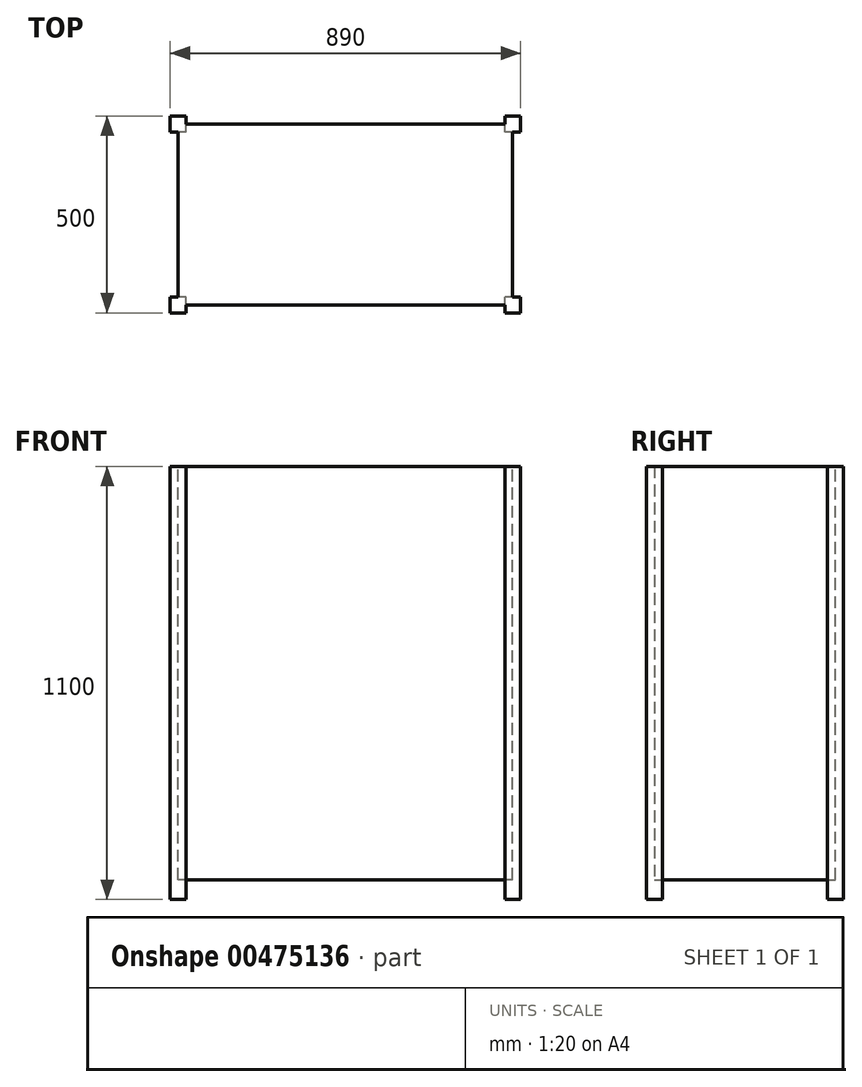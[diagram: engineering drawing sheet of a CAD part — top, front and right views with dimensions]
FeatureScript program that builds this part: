
annotation { "Feature Type Name" : "Feature", "Feature Type Description" : "" }
export const myFeature = defineFeature(function(context is Context, id is Id, definition is map)
    precondition{}
    {
        {
            var Q0;
            Q0=qCreatedBy(makeId("Top.planeOp"),FACE);
            var sketch = newSketch(context, id + "F0", { "sketchPlane" : qUnion([Q0])});
            skLineSegment(sketch, "E0.bottom", {"start": v(425, -230) * mm, "end": v(-425, -230) * mm, "construction": true});
            skLineSegment(sketch, "E0.top", {"start": v(425, 230) * mm, "end": v(-425, 230) * mm, "construction": true});
            skLineSegment(sketch, "E0.left", {"start": v(425, -230) * mm, "end": v(425, 230) * mm, "construction": true});
            skLineSegment(sketch, "E0.right", {"start": v(-425, -230) * mm, "end": v(-425, 230) * mm, "construction": true});
            skPoint(sketch, "E0.middle", {"position": v(0, 0) * mm});
            skLineSegment(sketch, "E1.bottom", {"start": v(-405, 210) * mm, "end": v(-445, 210) * mm});
            skLineSegment(sketch, "E1.top", {"start": v(-405, 250) * mm, "end": v(-445, 250) * mm});
            skLineSegment(sketch, "E1.left", {"start": v(-405, 210) * mm, "end": v(-405, 250) * mm});
            skLineSegment(sketch, "E1.right", {"start": v(-445, 210) * mm, "end": v(-445, 250) * mm});
            skPoint(sketch, "E1.middle", {"position": v(-425, 230) * mm});
            skLineSegment(sketch, "E2.bottom", {"start": v(-405, -250) * mm, "end": v(-445, -250) * mm});
            skLineSegment(sketch, "E2.top", {"start": v(-405, -210) * mm, "end": v(-445, -210) * mm});
            skLineSegment(sketch, "E2.left", {"start": v(-405, -250) * mm, "end": v(-405, -210) * mm});
            skLineSegment(sketch, "E2.right", {"start": v(-445, -250) * mm, "end": v(-445, -210) * mm});
            skPoint(sketch, "E2.middle", {"position": v(-425, -230) * mm});
            skLineSegment(sketch, "E3.bottom", {"start": v(445, 210) * mm, "end": v(405, 210) * mm});
            skLineSegment(sketch, "E3.top", {"start": v(445, 250) * mm, "end": v(405, 250) * mm});
            skLineSegment(sketch, "E3.left", {"start": v(445, 210) * mm, "end": v(445, 250) * mm});
            skLineSegment(sketch, "E3.right", {"start": v(405, 210) * mm, "end": v(405, 250) * mm});
            skPoint(sketch, "E3.middle", {"position": v(425, 230) * mm});
            skLineSegment(sketch, "E4.bottom", {"start": v(445, -250) * mm, "end": v(405, -250) * mm});
            skLineSegment(sketch, "E4.top", {"start": v(445, -210) * mm, "end": v(405, -210) * mm});
            skLineSegment(sketch, "E4.left", {"start": v(445, -250) * mm, "end": v(445, -210) * mm});
            skLineSegment(sketch, "E4.right", {"start": v(405, -250) * mm, "end": v(405, -210) * mm});
            skPoint(sketch, "E4.middle", {"position": v(425, -230) * mm});
            skSolve(sketch);
        }
        {
            var Q0;
            Q0=makeQuery(id+"F0.imprint","IMPRINT",FACE,{"disambiguationData":[TD([[makeQuery(id+"F0.imprint","IMPRINT",EDGE,{"derivedFrom":sQuery(id+"F0.wireOp",EDGE,"E1.bottom")}),-1.0]])]});
            var Q1;
            Q1=makeQuery(id+"F0.imprint","IMPRINT",FACE,{"disambiguationData":[TD([[makeQuery(id+"F0.imprint","IMPRINT",EDGE,{"derivedFrom":sQuery(id+"F0.wireOp",EDGE,"E2.bottom")}),-1.0]])]});
            var Q2;
            Q2=makeQuery(id+"F0.imprint","IMPRINT",FACE,{"disambiguationData":[TD([[makeQuery(id+"F0.imprint","IMPRINT",EDGE,{"derivedFrom":sQuery(id+"F0.wireOp",EDGE,"E4.bottom")}),-1.0]])]});
            var Q3;
            Q3=makeQuery(id+"F0.imprint","IMPRINT",FACE,{"disambiguationData":[TD([[makeQuery(id+"F0.imprint","IMPRINT",EDGE,{"derivedFrom":sQuery(id+"F0.wireOp",EDGE,"E3.bottom")}),-1.0]])]});
            extrude(context, id + "F1", {"entities" : qUnion([Q0, Q1, Q2, Q3]), "depth" : 1100 * mm});
        }
        {
            var Q0;
            Q0=makeQuery(id+"F1.opExtrude","CAP_FACE",FACE,{"disambiguationData":[OSD([sQuery(id+"F0.wireOp",EDGE,"E1.bottom"),sQuery(id+"F0.wireOp",EDGE,"E1.top"),sQuery(id+"F0.wireOp",EDGE,"E1.left"),sQuery(id+"F0.wireOp",EDGE,"E1.right")])],"isStart":false});
            var sketch = newSketch(context, id + "F2", { "sketchPlane" : qUnion([Q0])});
            skLineSegment(sketch, "E5.0", {"start": v(425, 230) * mm, "end": v(-425, 230) * mm});
            skLineSegment(sketch, "E5.1", {"start": v(-425, -230) * mm, "end": v(-425, 230) * mm});
            skLineSegment(sketch, "E5.2", {"start": v(425, -230) * mm, "end": v(-425, -230) * mm});
            skLineSegment(sketch, "E5.3", {"start": v(425, -230) * mm, "end": v(425, 230) * mm});
            skSolve(sketch);
        }
        {
            var Q0;
            {var subQ0=sQuery(id+"F2.wireOp",EDGE,"E5.2");Q0=makeQuery(id+"F2.imprint","IMPRINT",FACE,{"disambiguationData":[TD([[makeQuery(id+"F2.imprint","IMPRINT",EDGE,{"derivedFrom":subQ0}),-1.0]])]});}
            extrude(context, id + "F3", {"entities" : qUnion([Q0]), "operationType" : NewBodyOperationType.ADD, "oppositeDirection" : true, "depth" : 1050 * mm});
        }
    });
